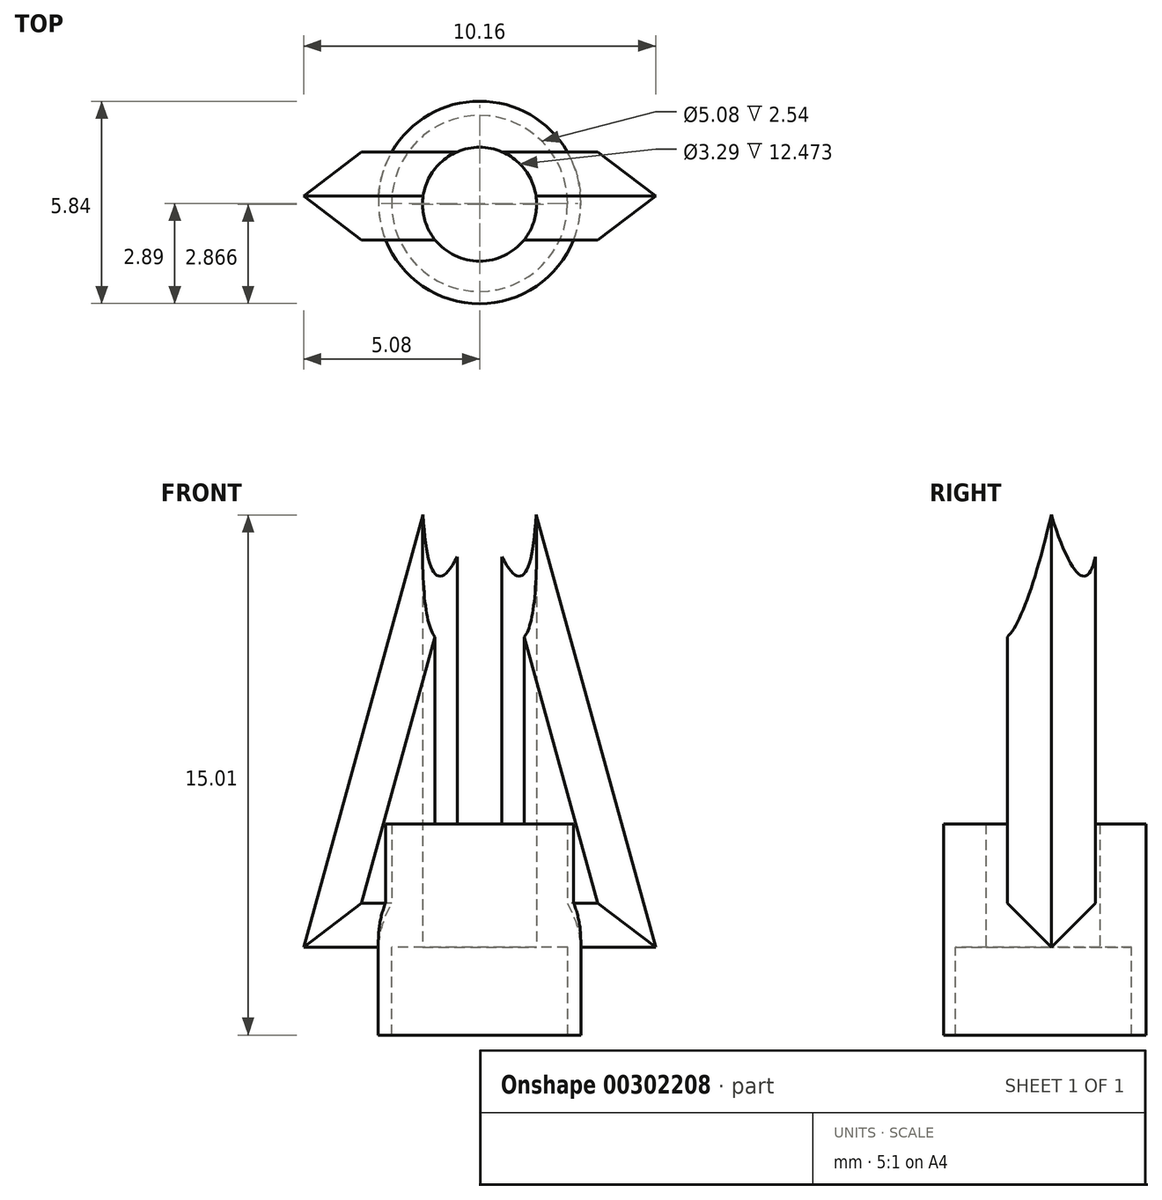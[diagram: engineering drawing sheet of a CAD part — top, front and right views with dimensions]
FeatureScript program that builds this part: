
annotation { "Feature Type Name" : "Feature", "Feature Type Description" : "" }
export const myFeature = defineFeature(function(context is Context, id is Id, definition is map)
    precondition{}
    {
        {
            var Q0;
            Q0=qCreatedBy(makeId("Front.planeOp"),FACE);
            var sketch = newSketch(context, id + "F0", { "sketchPlane" : qUnion([Q0])});
            skLineSegment(sketch, "E0", {"start": v(-5.08, 0) * mm, "end": v(0, 18.35) * mm});
            skLineSegment(sketch, "E1", {"start": v(0, 18.35) * mm, "end": v(5.08, 0) * mm});
            skLineSegment(sketch, "E2", {"start": v(5.08, 0) * mm, "end": v(-5.08, 0) * mm});
            skSolve(sketch);
        }
        {
            var Q0;
            Q0 = qSketchRegion(id + "F0", true);
            extrude(context, id + "F1", {"entities" : qUnion([Q0]), "depth" : 2.54 * mm});
        }
        {
            var Q0;
            Q0=makeQuery(id+"F1.opExtrude","CAP_EDGE",EDGE,{"disambiguationData":[OSD([sQuery(id+"F0.wireOp",EDGE,"E1")])],"isStart":false});
            var Q1;
            Q1=makeQuery(id+"F1.opExtrude","CAP_EDGE",EDGE,{"disambiguationData":[OSD([sQuery(id+"F0.wireOp",EDGE,"E0")])],"isStart":false});
            var Q2;
            Q2=makeQuery(id+"F1.opExtrude","CAP_EDGE",EDGE,{"disambiguationData":[OSD([sQuery(id+"F0.wireOp",EDGE,"E0")])],"isStart":true});
            var Q3;
            Q3=makeQuery(id+"F1.opExtrude","CAP_EDGE",EDGE,{"disambiguationData":[OSD([sQuery(id+"F0.wireOp",EDGE,"E1")])],"isStart":true});
            var Q4;
            Q4=makeQuery(id+"F1.opExtrude","CAP_EDGE",EDGE,{"disambiguationData":[OSD([sQuery(id+"F0.wireOp",EDGE,"E2")])],"isStart":true});
            var Q5;
            Q5=makeQuery(id+"F1.opExtrude","CAP_EDGE",EDGE,{"disambiguationData":[OSD([sQuery(id+"F0.wireOp",EDGE,"E2")])],"isStart":false});
            chamfer(context, id + "F2", {"entities" : qUnion([Q0, Q1, Q2, Q3, Q4, Q5]), "width" : 1.27 * mm, "tangentPropagation" : true});
        }
        {
            var Q0;
            Q0=qCreatedBy(makeId("Top.planeOp"),FACE);
            var sketch = newSketch(context, id + "F3", { "sketchPlane" : qUnion([Q0])});
            skCircle(sketch, "E3", {"center": v(0, -1.46) * mm, "radius": 2.92 * mm});
            skSolve(sketch);
        }
        {
            var Q0;
            Q0=makeQuery(id+"F3.imprint","IMPRINT",FACE,{"disambiguationData":[TD([[makeQuery(id+"F3.imprint","IMPRINT",EDGE,{"derivedFrom":sQuery(id+"F3.wireOp",EDGE,"E3")}),1.0]])]});
            extrude(context, id + "F4", {"entities" : qUnion([Q0]), "operationType" : NewBodyOperationType.ADD, "depth" : 3.56 * mm, "hasSecondDirection" : true, "secondDirectionOppositeDirection" : true, "secondDirectionDepth" : 2.54 * mm});
        }
        {
            var Q0;
            Q0=qCreatedBy(makeId("Top.planeOp"),FACE);
            var sketch = newSketch(context, id + "F5", { "sketchPlane" : qUnion([Q0])});
            skCircle(sketch, "E4", {"center": v(0, -1.49) * mm, "radius": 2.54 * mm});
            skSolve(sketch);
        }
        {
            var Q0;
            Q0 = qSketchRegion(id + "F5", true);
            extrude(context, id + "F6", {"entities" : qUnion([Q0]), "operationType" : NewBodyOperationType.REMOVE, "oppositeDirection" : true, "depth" : 25.4 * mm});
        }
        {
            var Q0;
            Q0=qCreatedBy(makeId("Top.planeOp"),FACE);
            var sketch = newSketch(context, id + "F7", { "sketchPlane" : qUnion([Q0])});
            skCircle(sketch, "E5", {"center": v(0, -1.51) * mm, "radius": 1.65 * mm});
            skSolve(sketch);
        }
        {
            var Q0;
            Q0 = qSketchRegion(id + "F7", true);
            extrude(context, id + "F8", {"entities" : qUnion([Q0]), "operationType" : NewBodyOperationType.REMOVE, "depth" : 25.4 * mm});
        }
    });
